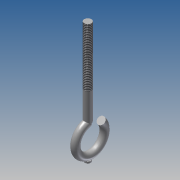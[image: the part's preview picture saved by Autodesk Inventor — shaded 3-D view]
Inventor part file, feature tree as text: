
AUTODESK INVENTOR PART (.ipt)
format: ipt  version: 2014 SP1 (Build 180222100, 222)  size: 179,712 bytes
history: native  units: in
note: dims shown in document units (in); Inventor stores cm internally (conversion verified against a paired STEP export)
features: sketch x4, plane x3, extrude x2, fillet x2, revolve x1, thread x1
ambient origin geometry x8: Origin, YZ Plane, XZ Plane, XY Plane, X Axis, Y Axis, Z Axis, Center Point
bodies: Solid1 (feature_tree)
feature tree (13):
  extrude  "Extrusion1"  Depth=1.5in TaperAngle=0.0deg
  sketch  "Sketch2"  dims[d15=-0.1in d17=0.125in d18=0.25in d19=2.1301in d20=0.125in]
  plane  "Work Plane1"
  plane  "Work Plane2"
  revolve  "Revolution1"  [1 undecoded]
  thread  "Thread5"  [1 undecoded]
  fillet  "Fillet1"  Radius=2.1301in
  fillet  "Fillet2"  Radius=0.125in
  plane  "Work Plane3"
  extrude  "Extrusion2"  Depth=0.05in
  sketch  "Sketch1"  dims[d0=0.125in d2=1.5in d3=0.0in]
  sketch  "Sketch5"  dims[d21=1.0in d22=0.0in d23=0.05in]
  sketch  "Sketch6"  dims[d24=0.03in d25=-0.55in d26=0.1in d27=0.03in d28=0.0in]
note: 2 required parameter values undecoded (feature->parameter linkage not recoverable at this tier; creation-order binding heuristic only, values carry confidence <= 0.55)